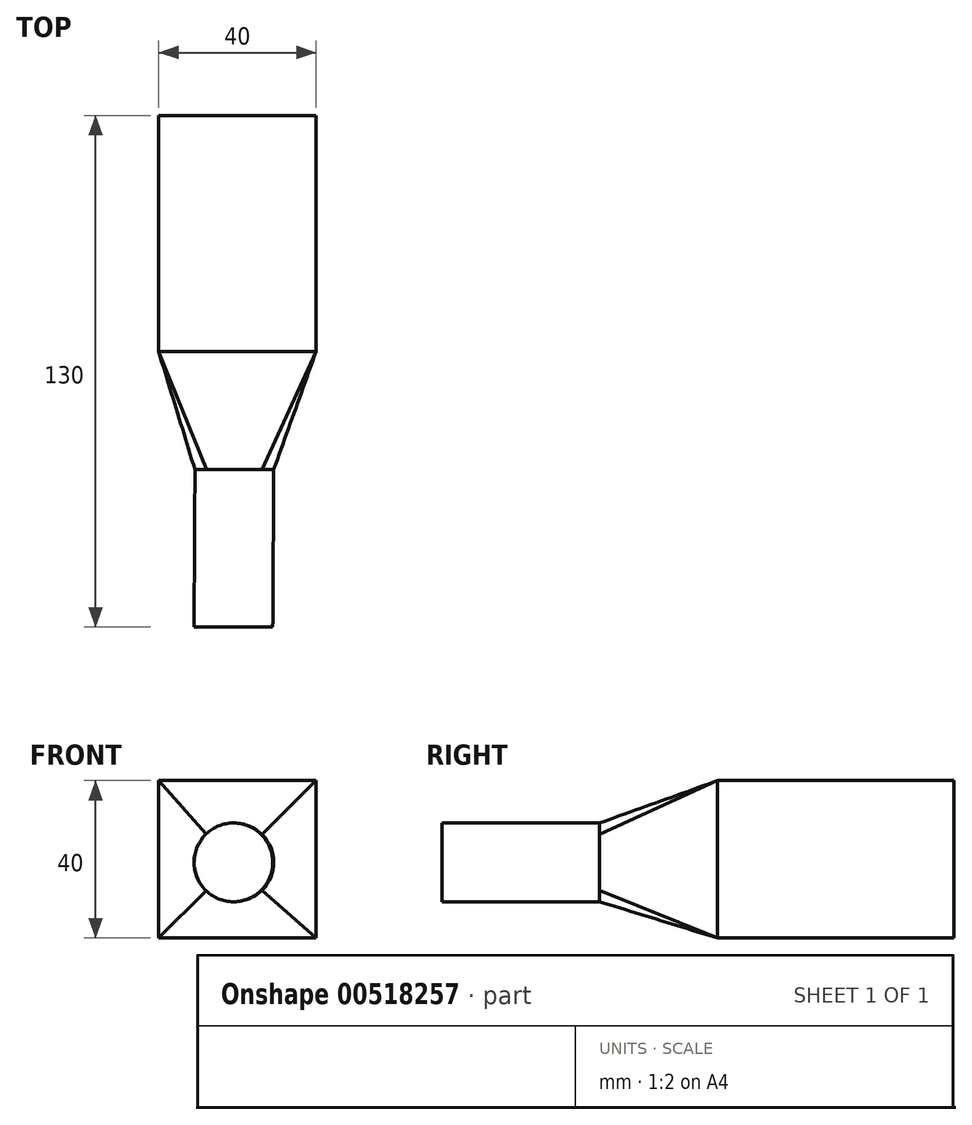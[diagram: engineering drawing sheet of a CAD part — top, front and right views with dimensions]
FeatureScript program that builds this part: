
annotation { "Feature Type Name" : "Feature", "Feature Type Description" : "" }
export const myFeature = defineFeature(function(context is Context, id is Id, definition is map)
    precondition{}
    {
        {
            var Q0;
            Q0=qCreatedBy(makeId("Front.planeOp"),FACE);
            var sketch = newSketch(context, id + "F0", { "sketchPlane" : qUnion([Q0])});
            skLineSegment(sketch, "E0.bottom", {"start": v(0, 0) * mm, "end": v(40, 0) * mm});
            skLineSegment(sketch, "E0.top", {"start": v(0, 40) * mm, "end": v(40, 40) * mm});
            skLineSegment(sketch, "E0.left", {"start": v(0, 0) * mm, "end": v(0, 40) * mm});
            skLineSegment(sketch, "E0.right", {"start": v(40, 0) * mm, "end": v(40, 40) * mm});
            skSolve(sketch);
        }
        {
            var Q0;
            Q0=qCreatedBy(makeId("Front.planeOp"),FACE);
            cPlane(context, id + "F1", {"entities" : qUnion([Q0]), "cplaneType" : CPlaneType.OFFSET, "offset" : 60 * mm, "width" : 150 * mm, "height" : 150 * mm});
        }
        {
            var Q0;
            Q0=qCreatedBy(id+"F1.planeOp",FACE);
            var sketch = newSketch(context, id + "F2", { "sketchPlane" : qUnion([Q0])});
            skLineSegment(sketch, "E1.bottom", {"start": v(0, 0) * mm, "end": v(40, 0) * mm});
            skLineSegment(sketch, "E1.top", {"start": v(0, 40) * mm, "end": v(40, 40) * mm});
            skLineSegment(sketch, "E1.left", {"start": v(0, 0) * mm, "end": v(0, 40) * mm});
            skLineSegment(sketch, "E1.right", {"start": v(40, 0) * mm, "end": v(40, 40) * mm});
            skSolve(sketch);
        }
        {
            var Q0;
            Q0=qCreatedBy(makeId("Front.planeOp"),FACE);
            cPlane(context, id + "F3", {"entities" : qUnion([Q0]), "cplaneType" : CPlaneType.OFFSET, "offset" : 90 * mm, "width" : 150 * mm, "height" : 150 * mm});
        }
        {
            var Q0;
            Q0=qCreatedBy(id+"F3.planeOp",FACE);
            var sketch = newSketch(context, id + "F4", { "sketchPlane" : qUnion([Q0])});
            skCircle(sketch, "E2", {"center": v(19.23, 19.23) * mm, "radius": 10 * mm});
            skSolve(sketch);
        }
        {
            var Q0;
            Q0=qCreatedBy(makeId("Front.planeOp"),FACE);
            cPlane(context, id + "F5", {"entities" : qUnion([Q0]), "cplaneType" : CPlaneType.OFFSET, "offset" : 130 * mm, "width" : 150 * mm, "height" : 150 * mm});
        }
        {
            var Q0;
            Q0=qCreatedBy(id+"F5.planeOp",FACE);
            var sketch = newSketch(context, id + "F6", { "sketchPlane" : qUnion([Q0])});
            skCircle(sketch, "E3", {"center": v(19, 19.23) * mm, "radius": 10 * mm});
            skSolve(sketch);
        }
        {
            var Q0;
            Q0=makeQuery(id+"F0.imprint","IMPRINT",FACE,{"disambiguationData":[TD([[makeQuery(id+"F0.imprint","IMPRINT",EDGE,{"derivedFrom":sQuery(id+"F0.wireOp",EDGE,"E0.bottom")}),1.0]])]});
            var Q1;
            Q1=makeQuery(id+"F2.imprint","IMPRINT",FACE,{"disambiguationData":[TD([[makeQuery(id+"F2.imprint","IMPRINT",EDGE,{"derivedFrom":sQuery(id+"F2.wireOp",EDGE,"E1.bottom")}),1.0]])]});
            loft(context, id + "F7", {"sheetProfilesArray" : [{ "sheetProfileEntities" : qUnion([Q0]) }, { "sheetProfileEntities" : qUnion([Q1]) }]});
        }
        {
            var Q1;
            Q1=makeQuery(id+"F7.opLoft","CAP_FACE",FACE,{"disambiguationData":[OSD([makeQuery(id+"F2.imprint","IMPRINT",FACE,{"disambiguationData":[TD([[makeQuery(id+"F2.imprint","IMPRINT",EDGE,{"derivedFrom":sQuery(id+"F2.wireOp",EDGE,"E1.bottom")}),1.0]])]})])],"isStart":true});
            var Q2;
            Q2=makeQuery(id+"F4.imprint","IMPRINT",FACE,{"disambiguationData":[TD([[makeQuery(id+"F4.imprint","IMPRINT",EDGE,{"derivedFrom":sQuery(id+"F4.wireOp",EDGE,"E2")}),1.0]])]});
            loft(context, id + "F8", {"operationType" : NewBodyOperationType.ADD, "sheetProfilesArray" : [{ "sheetProfileEntities" : qUnion([Q1]) }, { "sheetProfileEntities" : qUnion([Q2]) }]});
        }
        {
            var Q1;
            Q1=makeQuery(id+"F8.opLoft","CAP_FACE",FACE,{"disambiguationData":[OSD([makeQuery(id+"F4.imprint","IMPRINT",FACE,{"disambiguationData":[TD([[makeQuery(id+"F4.imprint","IMPRINT",EDGE,{"derivedFrom":sQuery(id+"F4.wireOp",EDGE,"E2")}),1.0]])]})])],"isStart":true});
            var Q2;
            Q2=makeQuery(id+"F6.imprint","IMPRINT",FACE,{"disambiguationData":[TD([[makeQuery(id+"F6.imprint","IMPRINT",EDGE,{"derivedFrom":sQuery(id+"F6.wireOp",EDGE,"E3")}),1.0]])]});
            loft(context, id + "F9", {"operationType" : NewBodyOperationType.ADD, "sheetProfilesArray" : [{ "sheetProfileEntities" : qUnion([Q1]) }, { "sheetProfileEntities" : qUnion([Q2]) }]});
        }
    });
